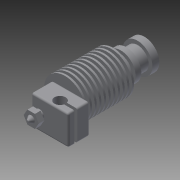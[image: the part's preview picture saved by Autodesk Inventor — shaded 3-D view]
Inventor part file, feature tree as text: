
AUTODESK INVENTOR PART (.ipt)
format: ipt  version: 2013 (Build 170138000, 138)  size: 297,472 bytes
history: native  units: mm
features: sketch x8, extrude x5, revolve x3, projected_geometry x2, pattern_linear x1, fillet x1
ambient origin geometry x8: Origin, YZ Plane, XZ Plane, XY Plane, X Axis, Y Axis, Z Axis, Center Point
bodies: Solid1 (feature_tree)
feature tree (20):
  revolve  "Revolution1"  [1 undecoded]
  revolve  "Revolution2"  [1 undecoded]
  pattern_linear  "Rectangular Pattern1"  Spacing1=1.0mm  [1 undecoded]
  extrude  "Extrusion1"  TaperAngle=90.0deg  [1 undecoded]
  extrude  "Extrusion2"  Depth=120.0mm
  extrude  "Extrusion3"  Depth=2.8mm
  extrude  "Extrusion4"  Depth=2.1mm TaperAngle=0.0deg
  fillet  "Fillet1"  Radius=4.5mm
  extrude  "Extrusion5"  Depth=16.0mm
  revolve  "Revolution3"  [1 undecoded]
  sketch  "Sketch1"  dims[d0=6.0mm d2=8.0mm]
  sketch  "Sketch2"  dims[d3=11.15mm d4=26.0mm]
  sketch  "Sketch3"  dims[d5=42.7mm]
  sketch  "Sketch4"  dims[d6=3.7mm]
  sketch  "Sketch5"  dims[d7=6.0mm]
  sketch  "Sketch6"  dims[d8=90.0deg]
  sketch  "Sketch7"  dims[d9=6.0mm]
  sketch  "Sketch8"  dims[d10=1.5mm d11=1.0mm d12=90.0deg d13=120.0mm d15=2.5mm d16=2.8mm d18=2.1mm d19=0.0mm d20=4.5mm d21=16.0mm d22=20.0mm d23=11.5mm d24=0.0mm d25=4.0mm d26=6.0mm d27=1.5mm d28=11.5mm d29=11.5mm d30=0.0mm d31=1.0mm d32=5.0mm d34=1.5mm d35=0.0mm d36=7.0mm d37=3.0mm d38=0.0mm d39=21.816616mm d41=0.5mm d42=2.0mm d43=90.0deg]
  projected_geometry  "Project Cut Edges1"
  projected_geometry  "Project Cut Edges2"
note: 5 required parameter values undecoded (feature->parameter linkage not recoverable at this tier; creation-order binding heuristic only, values carry confidence <= 0.55)